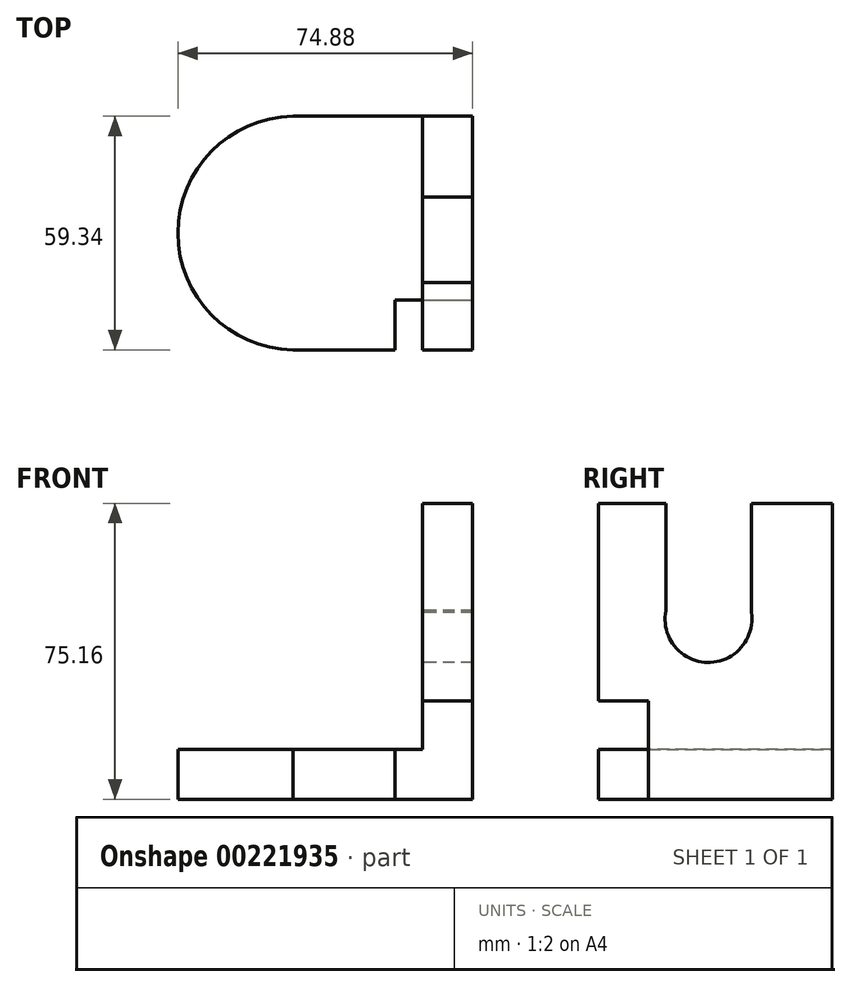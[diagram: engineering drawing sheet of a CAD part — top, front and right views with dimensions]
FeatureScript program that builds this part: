
annotation { "Feature Type Name" : "Feature", "Feature Type Description" : "" }
export const myFeature = defineFeature(function(context is Context, id is Id, definition is map)
    precondition{}
    {
        {
            var Q0;
            Q0=qCreatedBy(makeId("Top.planeOp"),FACE);
            var sketch = newSketch(context, id + "F0", { "sketchPlane" : qUnion([Q0])});
            skArc(sketch, "E0", {"start": v(0, -7.62) * mm, "mid": v(-29.17, -37.3) * mm, "end": v(0, -66.96) * mm});
            skLineSegment(sketch, "E1.bottom", {"start": v(0, -66.96) * mm, "end": v(33, -66.96) * mm});
            skLineSegment(sketch, "E1.top", {"start": v(0, -7.62) * mm, "end": v(33, -7.62) * mm});
            skLineSegment(sketch, "E1.left", {"start": v(0, -66.96) * mm, "end": v(0, -7.62) * mm});
            skLineSegment(sketch, "E1.right", {"start": v(33, -66.96) * mm, "end": v(33, -7.62) * mm});
            skSolve(sketch);
        }
        {
            var Q0;
            Q0 = qSketchRegion(id + "F0", true);
            extrude(context, id + "F1", {"entities" : qUnion([Q0]), "depth" : 12.7 * mm});
        }
        {
            var Q0;
            Q0=makeQuery(id+"F1.opExtrude","SWEPT_FACE",FACE,{"disambiguationData":[OSD([sQuery(id+"F0.wireOp",EDGE,"E1.right")])]});
            var sketch = newSketch(context, id + "F2", { "sketchPlane" : qUnion([Q0])});
            skLineSegment(sketch, "E2.bottom", {"start": v(-66.96, 0) * mm, "end": v(-7.62, 0) * mm});
            skLineSegment(sketch, "E2.top", {"start": v(-66.96, 75.16) * mm, "end": v(-7.62, 75.16) * mm});
            skLineSegment(sketch, "E2.left", {"start": v(-66.96, 0) * mm, "end": v(-66.96, 75.16) * mm});
            skLineSegment(sketch, "E2.right", {"start": v(-7.62, 0) * mm, "end": v(-7.62, 75.16) * mm});
            skSolve(sketch);
        }
        {
            var Q0;
            Q0 = qSketchRegion(id + "F2", true);
            extrude(context, id + "F3", {"entities" : qUnion([Q0]), "operationType" : NewBodyOperationType.ADD, "depth" : 12.7 * mm});
        }
        {
            var Q0;
            Q0=makeQuery(id+"F3.opExtrude","CAP_FACE",FACE,{"disambiguationData":[OSD([sQuery(id+"F2.wireOp",EDGE,"E2.bottom"),sQuery(id+"F2.wireOp",EDGE,"E2.top"),sQuery(id+"F2.wireOp",EDGE,"E2.left"),sQuery(id+"F2.wireOp",EDGE,"E2.right")])],"isStart":true});
            var sketch = newSketch(context, id + "F4", { "sketchPlane" : qUnion([Q0])});
            skArc(sketch, "E3", {"start": v(28.17, 47.45) * mm, "mid": v(39.3, 34.75) * mm, "end": v(49.88, 47.91) * mm});
            skLineSegment(sketch, "E4", {"start": v(28.17, 47.45) * mm, "end": v(28.17, 75.16) * mm});
            skLineSegment(sketch, "E5", {"start": v(28.17, 75.16) * mm, "end": v(49.88, 75.16) * mm});
            skLineSegment(sketch, "E6", {"start": v(49.88, 75.16) * mm, "end": v(49.88, 47.91) * mm});
            skSolve(sketch);
        }
        {
            var Q0;
            Q0 = qSketchRegion(id + "F4", true);
            extrude(context, id + "F5", {"entities" : qUnion([Q0]), "operationType" : NewBodyOperationType.REMOVE, "endBound" : BoundingType.THROUGH_ALL, "oppositeDirection" : true, "depth" : 25.4 * mm});
        }
        {
            var Q0;
            Q0=makeQuery(id+"F3.boolean.opBoolean","MERGE",FACE,{"derivedFrom":[makeQuery(id+"F1.opExtrude","SWEPT_FACE",FACE,{"disambiguationData":[OSD([sQuery(id+"F0.wireOp",EDGE,"E1.bottom")])]}),makeQuery(id+"F3.opExtrude","SWEPT_FACE",FACE,{"disambiguationData":[OSD([sQuery(id+"F2.wireOp",EDGE,"E2.left")])]})]});
            var sketch = newSketch(context, id + "F6", { "sketchPlane" : qUnion([Q0])});
            skLineSegment(sketch, "E7.bottom", {"start": v(25.94, 12.7) * mm, "end": v(45.7, 12.7) * mm});
            skLineSegment(sketch, "E7.top", {"start": v(25.94, 0) * mm, "end": v(45.7, 0) * mm});
            skLineSegment(sketch, "E7.left", {"start": v(25.94, 12.7) * mm, "end": v(25.94, 0) * mm});
            skLineSegment(sketch, "E7.right", {"start": v(45.7, 12.7) * mm, "end": v(45.7, 0) * mm});
            skLineSegment(sketch, "E8.bottom", {"start": v(33, 12.7) * mm, "end": v(45.7, 12.7) * mm});
            skLineSegment(sketch, "E8.top", {"start": v(33, 25) * mm, "end": v(45.7, 25) * mm});
            skLineSegment(sketch, "E8.left", {"start": v(33, 12.7) * mm, "end": v(33, 25) * mm});
            skLineSegment(sketch, "E8.right", {"start": v(45.7, 12.7) * mm, "end": v(45.7, 25) * mm});
            skSolve(sketch);
        }
        {
            var Q0;
            Q0 = qSketchRegion(id + "F6", true);
            extrude(context, id + "F7", {"entities" : qUnion([Q0]), "operationType" : NewBodyOperationType.REMOVE, "oppositeDirection" : true, "depth" : 12.7 * mm});
        }
    });
